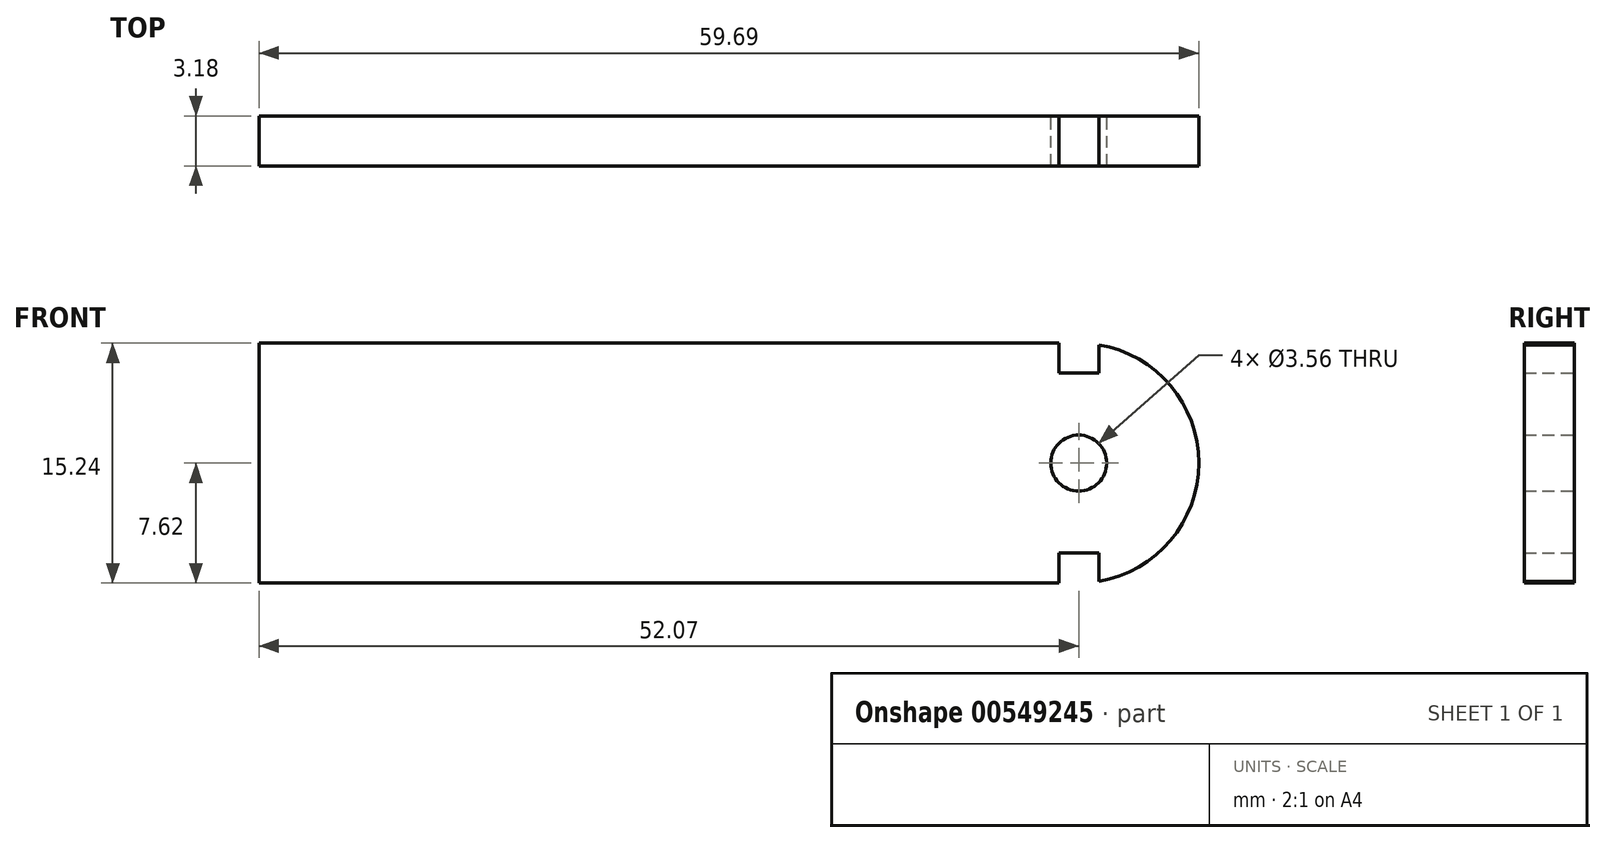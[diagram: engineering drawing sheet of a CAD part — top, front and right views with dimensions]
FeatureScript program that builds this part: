
annotation { "Feature Type Name" : "Feature", "Feature Type Description" : "" }
export const myFeature = defineFeature(function(context is Context, id is Id, definition is map)
    precondition{}
    {
        {
            var Q0;
            Q0=qCreatedBy(makeId("Front.planeOp"),FACE);
            var sketch = newSketch(context, id + "F0", { "sketchPlane" : qUnion([Q0])});
            skLineSegment(sketch, "E0.bottom", {"start": v(17.78, 3.81) * mm, "end": v(-33.02, 3.81) * mm});
            skLineSegment(sketch, "E0.top", {"start": v(17.78, -11.43) * mm, "end": v(-33.02, -11.43) * mm});
            skLineSegment(sketch, "E0.right", {"start": v(-33.02, 3.81) * mm, "end": v(-33.02, -11.43) * mm});
            skPoint(sketch, "E0.middle", {"position": v(0, 0) * mm});
            skArc(sketch, "E1", {"start": v(20.32, -11.32) * mm, "mid": v(26.67, -3.8) * mm, "end": v(20.32, 3.7) * mm});
            skCircle(sketch, "E2", {"center": v(19.05, -3.8) * mm, "radius": 1.78 * mm});
            skLineSegment(sketch, "E3.bottom", {"start": v(17.78, 1.9) * mm, "end": v(20.32, 1.9) * mm});
            skLineSegment(sketch, "E3.left", {"start": v(17.78, 1.9) * mm, "end": v(17.78, 3.81) * mm});
            skLineSegment(sketch, "E3.right", {"start": v(20.32, 1.9) * mm, "end": v(20.32, 3.7) * mm});
            skLineSegment(sketch, "E4", {"start": v(19.05, -3.8) * mm, "end": v(15.42, -3.8) * mm, "construction": true});
            skLineSegment(sketch, "E5.MirrorCS", {"start": v(17.78, -9.52) * mm, "end": v(17.78, -11.43) * mm});
            skLineSegment(sketch, "E6.MirrorCS", {"start": v(17.78, -9.52) * mm, "end": v(20.32, -9.52) * mm});
            skLineSegment(sketch, "E7.MirrorCS", {"start": v(20.32, -9.52) * mm, "end": v(20.32, -11.32) * mm});
            skSolve(sketch);
        }
        {
            var Q0;
            Q0 = qSketchRegion(id + "F0", true);
            extrude(context, id + "F1", {"entities" : qUnion([Q0]), "depth" : 3.17 * mm, "offsetDistance" : 25.4 * mm});
        }
    });
